# Revit family: 01-3908-02 MONOMANDO LAVAPLATOS TIRSO
name_source: partatom
category: Aparatos sanitarios
units: mm (PartAtom-declared; Revit-internal decimal feet)

## family parameters
Anfitrión = Cara
Compartido = No
Corte con vacíos al cargar = No
Cota de conector redondo = Diámetro de uso
Número OmniClass = 23.31.11.00
Punto de cálculo de habitación = No
Tipo de pieza = Normal

## types (1)
- 01-3908-01
    Alto = 343 mm  [stored 1.12533 ft]
    Alto - aireador = 154 mm  [stored 0.505249 ft]
    Alto base = 103 mm  [stored 0.337927 ft]
    Ancho - aireador = 235 mm  [stored 0.770997 ft]
    Conexión AC = Sí
    Conexión AF = Sí
    Conexión de residuos = No
    Conexión de ventilación = No
    Descripción = Monomando
    Dim base = 42 mm
    Elevación por defecto = 0 mm  [stored 0 ft]
    Fabricante = Gricol
    Imagen de tipo = MONOMANDO LAVAPLATOS TIRSO.PNG
    Metal Laton Cromado = Metal Laton Cromado
    Metal Zamak Cromado = Metal Zamak Cromado
    Modelo = 01-3908-01
    Plastico - ABS Cromado = Plastico - ABS  + Colorante rojo
    Product Name = MONOMANDO LAVAPLATOS TIRSO
    URL = https://www.gricol.com

note: [stored X ft] marks values corroborated as IEEE doubles in the binary element streams (Revit-internal decimal feet)

## geometry (parser evidence)
native form markers: Blend x4, Sweep x4
no freeform markers — native parametric forms only
